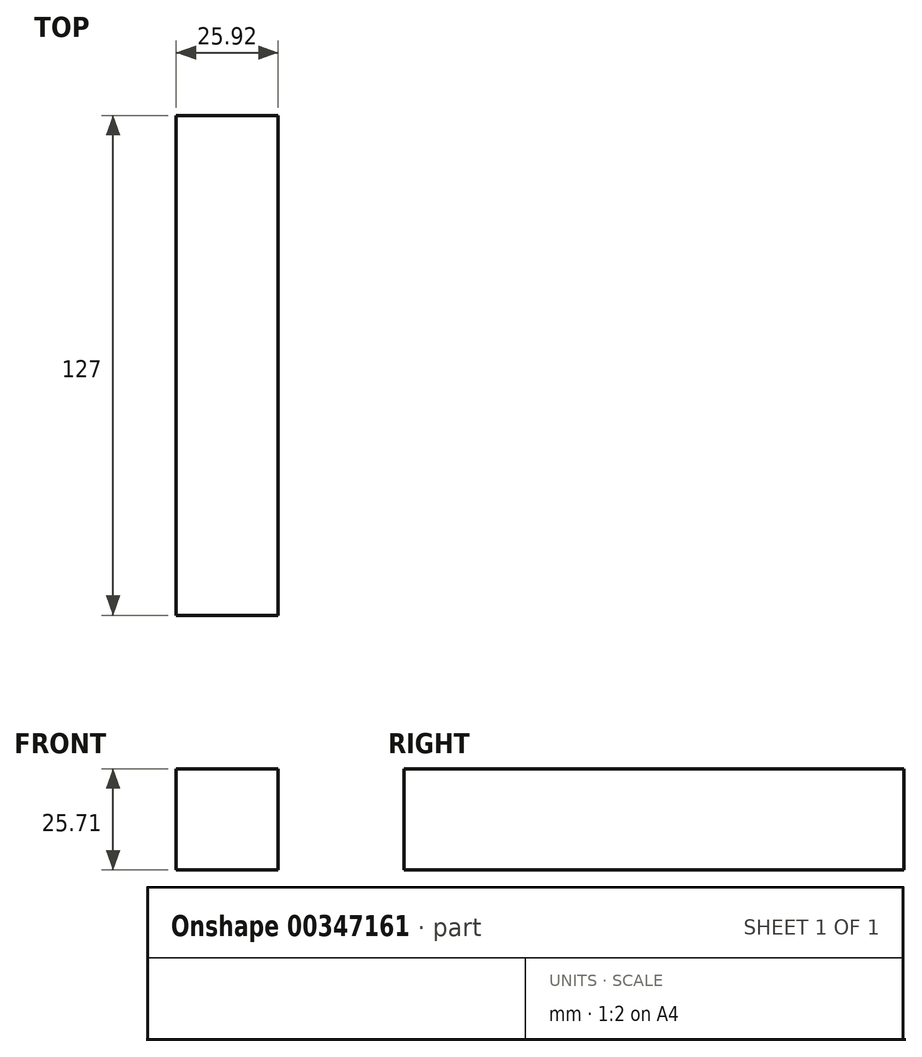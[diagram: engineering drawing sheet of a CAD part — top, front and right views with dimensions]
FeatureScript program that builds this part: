
annotation { "Feature Type Name" : "Feature", "Feature Type Description" : "" }
export const myFeature = defineFeature(function(context is Context, id is Id, definition is map)
    precondition{}
    {
        {
            var Q0;
            Q0=qCreatedBy(makeId("Front.planeOp"),FACE);
            var sketch = newSketch(context, id + "F0", { "sketchPlane" : qUnion([Q0])});
            skLineSegment(sketch, "E0.bottom", {"start": v(0, 0) * mm, "end": v(25.92, 0) * mm});
            skLineSegment(sketch, "E0.top", {"start": v(0, 25.71) * mm, "end": v(25.92, 25.71) * mm});
            skLineSegment(sketch, "E0.left", {"start": v(0, 0) * mm, "end": v(0, 25.71) * mm});
            skLineSegment(sketch, "E0.right", {"start": v(25.92, 0) * mm, "end": v(25.92, 25.71) * mm});
            skSolve(sketch);
        }
        {
            var Q0;
            Q0 = qSketchRegion(id + "F0", true);
            extrude(context, id + "F1", {"entities" : qUnion([Q0]), "oppositeDirection" : true, "depth" : 127 * mm});
        }
    });
